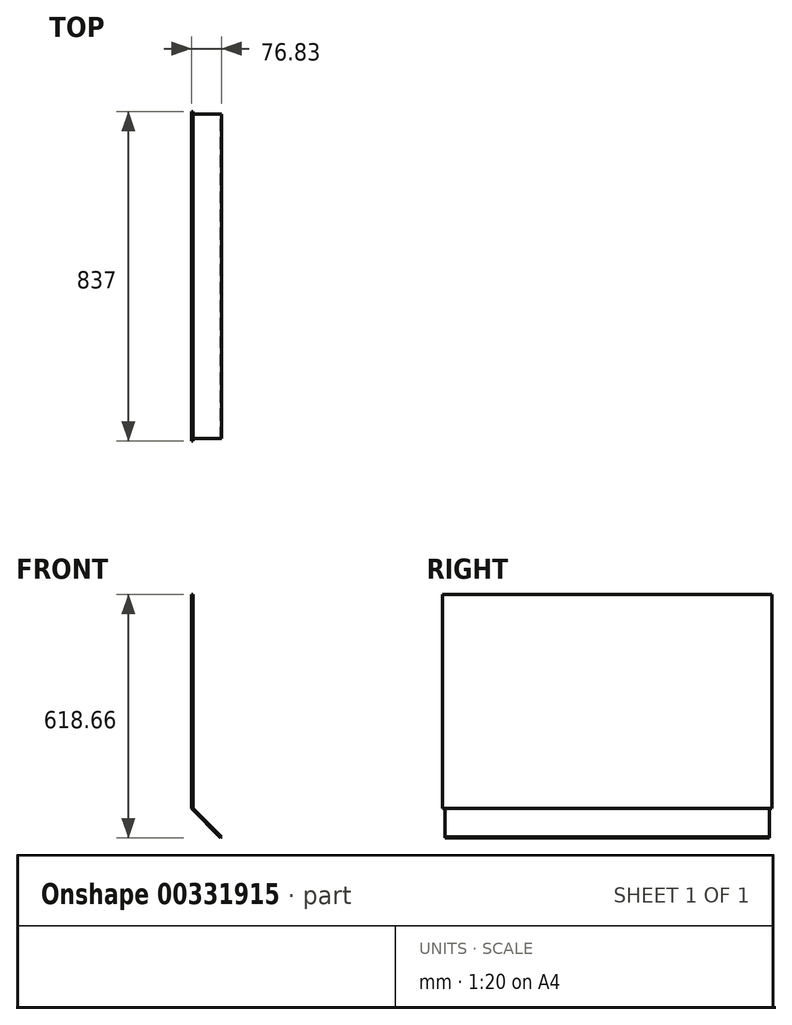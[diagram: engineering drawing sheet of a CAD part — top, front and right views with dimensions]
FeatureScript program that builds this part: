
annotation { "Feature Type Name" : "Feature", "Feature Type Description" : "" }
export const myFeature = defineFeature(function(context is Context, id is Id, definition is map)
    precondition{}
    {
        {
            var Q0;
            Q0=qCreatedBy(makeId("Front.planeOp"),FACE);
            var sketch = newSketch(context, id + "F0", { "sketchPlane" : qUnion([Q0])});
            skLineSegment(sketch, "E0.bottom", {"start": v(0, 0) * mm, "end": v(4, 0) * mm});
            skLineSegment(sketch, "E0.top", {"start": v(0, 543) * mm, "end": v(4, 543) * mm});
            skLineSegment(sketch, "E0.left", {"start": v(0, 0) * mm, "end": v(0, 543) * mm});
            skLineSegment(sketch, "E0.right", {"start": v(4, 0) * mm, "end": v(4, 543) * mm});
            skLineSegment(sketch, "E1", {"start": v(4, 0) * mm, "end": v(76.83, -72.83) * mm});
            skLineSegment(sketch, "E2", {"start": v(76.83, -72.83) * mm, "end": v(74, -75.66) * mm});
            skLineSegment(sketch, "E3", {"start": v(74, -75.66) * mm, "end": v(0, 0) * mm});
            skSolve(sketch);
        }
        {
            var Q0;
            Q0 = qSketchRegion(id + "F0", true);
            extrude(context, id + "F1", {"entities" : qUnion([Q0]), "depth" : 825 * mm});
        }
        {
            var Q0;
            Q0=makeQuery(id+"F1.opExtrude","SWEPT_FACE",FACE,{"disambiguationData":[OSD([sQuery(id+"F0.wireOp",EDGE,"E0.right")])]});
            var sketch = newSketch(context, id + "F2", { "sketchPlane" : qUnion([Q0])});
            skLineSegment(sketch, "E4.bottom", {"start": v(0, 543) * mm, "end": v(6, 543) * mm});
            skLineSegment(sketch, "E4.top", {"start": v(0, 0) * mm, "end": v(6, 0) * mm});
            skLineSegment(sketch, "E4.left", {"start": v(0, 543) * mm, "end": v(0, 0) * mm});
            skLineSegment(sketch, "E4.right", {"start": v(6, 543) * mm, "end": v(6, 0) * mm});
            skLineSegment(sketch, "E5.bottom", {"start": v(-825, 543) * mm, "end": v(-831, 543) * mm});
            skLineSegment(sketch, "E5.top", {"start": v(-825, 0) * mm, "end": v(-831, 0) * mm});
            skLineSegment(sketch, "E5.left", {"start": v(-825, 543) * mm, "end": v(-825, 0) * mm});
            skLineSegment(sketch, "E5.right", {"start": v(-831, 543) * mm, "end": v(-831, 0) * mm});
            skSolve(sketch);
        }
        {
            var Q0;
            Q0 = qSketchRegion(id + "F2", true);
            extrude(context, id + "F3", {"entities" : qUnion([Q0]), "operationType" : NewBodyOperationType.ADD, "oppositeDirection" : true, "depth" : 4 * mm});
        }
    });
